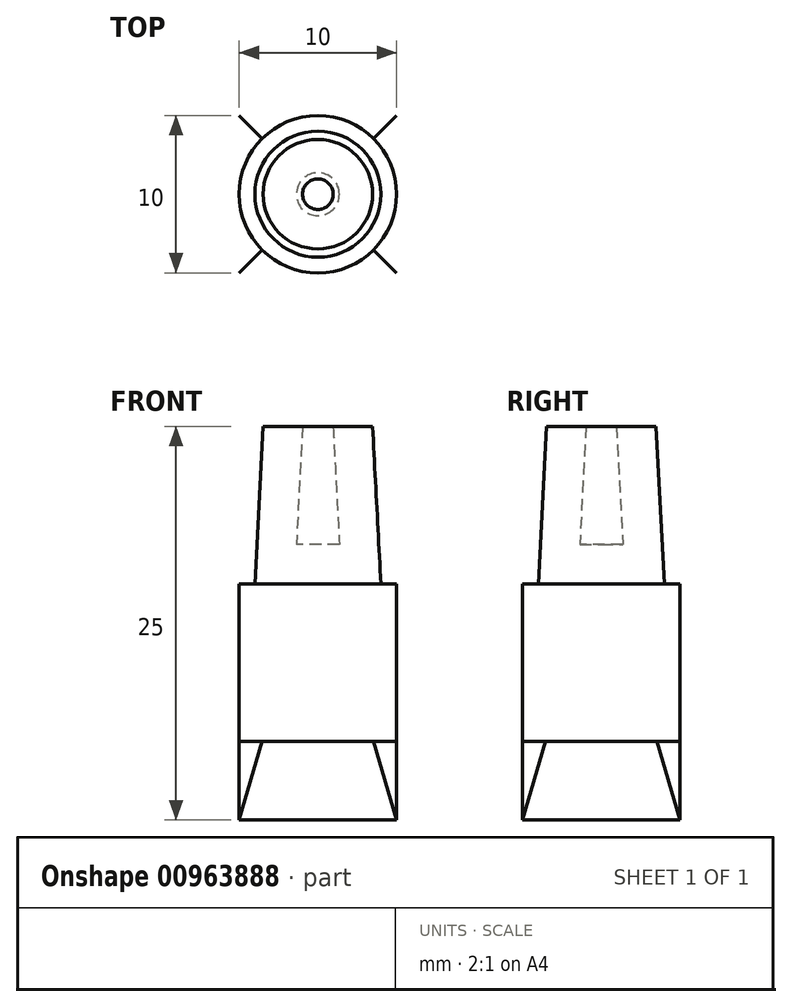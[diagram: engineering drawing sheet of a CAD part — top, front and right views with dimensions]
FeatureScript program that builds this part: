
annotation { "Feature Type Name" : "Feature", "Feature Type Description" : "" }
export const myFeature = defineFeature(function(context is Context, id is Id, definition is map)
    precondition{}
    {
        {
            var Q0;
            Q0=qCreatedBy(makeId("Top.planeOp"),FACE);
            var sketch = newSketch(context, id + "F0", { "sketchPlane" : qUnion([Q0])});
            skCircle(sketch, "E0", {"center": v(0, 0) * mm, "radius": 4 * mm});
            skSolve(sketch);
        }
        {
            var Q0;
            Q0=makeQuery(id+"F0.imprint","IMPRINT",FACE,{"disambiguationData":[TD([[makeQuery(id+"F0.imprint","IMPRINT",EDGE,{"derivedFrom":sQuery(id+"F0.wireOp",EDGE,"E0")}),1.0]])]});
            extrude(context, id + "F1", {"entities" : qUnion([Q0]), "depth" : 10 * mm, "offsetDistance" : 25 * mm, "hasDraft" : true, "draftAngle" : 3 * degree, "draftPullDirection" : true});
        }
        {
            var Q0;
            Q0=makeQuery(id+"F1.opExtrude","CAP_FACE",FACE,{"disambiguationData":[OSD([sQuery(id+"F0.wireOp",EDGE,"E0")])],"isStart":false});
            shell(context, id + "F2", {"entities" : qUnion([Q0]), "thickness" : 2.5 * mm});
        }
        {
            var Q0;
            Q0=makeQuery(id+"F1.opExtrude","CAP_FACE",FACE,{"disambiguationData":[OSD([sQuery(id+"F0.wireOp",EDGE,"E0")])],"isStart":true});
            var sketch = newSketch(context, id + "F3", { "sketchPlane" : qUnion([Q0])});
            skCircle(sketch, "E1", {"center": v(0, 0) * mm, "radius": 5 * mm});
            skSolve(sketch);
        }
        {
            var Q0;
            Q0 = qSketchRegion(id + "F3", true);
            extrude(context, id + "F4", {"entities" : qUnion([Q0]), "operationType" : NewBodyOperationType.ADD, "depth" : 10 * mm, "offsetDistance" : 25 * mm});
        }
        {
            var Q0;
            Q0=makeQuery(id+"F4.opExtrude","CAP_FACE",FACE,{"disambiguationData":[OSD([sQuery(id+"F3.wireOp",EDGE,"E1")])],"isStart":false});
            cPlane(context, id + "F5", {"entities" : qUnion([Q0]), "cplaneType" : CPlaneType.OFFSET, "offset" : 5 * mm, "width" : 150 * mm, "height" : 150 * mm});
        }
        {
            var Q0;
            Q0=qCreatedBy(id+"F5.planeOp",FACE);
            var sketch = newSketch(context, id + "F6", { "sketchPlane" : qUnion([Q0])});
            skLineSegment(sketch, "E2.bottom", {"start": v(-5, 5) * mm, "end": v(5, 5) * mm});
            skLineSegment(sketch, "E2.top", {"start": v(-5, -5) * mm, "end": v(5, -5) * mm});
            skLineSegment(sketch, "E2.left", {"start": v(-5, 5) * mm, "end": v(-5, -5) * mm});
            skLineSegment(sketch, "E2.right", {"start": v(5, 5) * mm, "end": v(5, -5) * mm});
            skPoint(sketch, "E2.middle", {"position": v(0, 0) * mm});
            skSolve(sketch);
        }
        {
            var Q0;
            Q0=makeQuery(id+"F4.opExtrude","CAP_FACE",FACE,{"disambiguationData":[OSD([sQuery(id+"F3.wireOp",EDGE,"E1")])],"isStart":false});
            var Q1;
            Q1=makeQuery(id+"F6.imprint","IMPRINT",FACE,{"disambiguationData":[TD([[makeQuery(id+"F6.imprint","IMPRINT",EDGE,{"derivedFrom":sQuery(id+"F6.wireOp",EDGE,"E2.bottom")}),-1.0]])]});
            loft(context, id + "F7", {"sheetProfilesArray" : [{ "sheetProfileEntities" : qUnion([Q0]) }, { "sheetProfileEntities" : qUnion([Q1]) }]});
        }
    });
